# Revit family: 3-108-fleet fan w-lighting fixture
name_source: partatom
category: Lighting Fixtures
units: mm (PartAtom-declared; Revit-internal decimal feet)

## family parameters
Always vertical = Yes
Cut with Voids When Loaded = No
Host = Ceiling
Light Source = Yes
Part Type = Normal
Room Calculation Point = No
Round Connector Dimension = Use Diameter
Shared = No

## types (7) — shared parameters
Color Filter = 16777215
Dimming Lamp Color Temperature Shift = <None>
Light Source Symbol Size = 610 mm
Main Diffuser = Matte White Acrylic
Manufacturer = Oxygen - Lighting & Fans
Model = 3-108-xx/37-108-xx Fleet Fan
References = Ref. 3 = 120 V / Ref. 37 = 277 V
URL = www.oxygenlighting.com
Voltage Input = 120 V or 277 V - 50/60 Hz

## per-type parameters (varying)
| type | Blade Finish | Metal Finish | Voltage |
| 3-108-15 / Black - Weathered Gray Blades | Weathered Gray Blades | 15 - Black | 120 V |
| 3-108-24 / Satin Nickel - Silver Blades | Silver | 24 - Satin Nickel | 120 V |
| 3-108-40 / Aged Brass - Matte Black | 15 - Black | 40 - Aged Brass | 120 V |
| 37-108-15 / Black - Weathered Gray Blades | Weathered Gray Blades | 15 - Black | 277 V |
| 37-108-24 / Satin Nickel - Silver Blades | Silver | 24 - Satin Nickel | 277 V |
| 37-108-40 / Aged Brass - Matte Black | 15 - Black | 40 - Aged Brass | 277 V |
| 37-108-24 / Satin Nickel - Silver | Silver | 24 - Satin Nickel | 277 V |

## geometry (parser evidence)
native form markers: Blend x10, Extrusion x2, Sweep x11
no freeform markers — native parametric forms only
